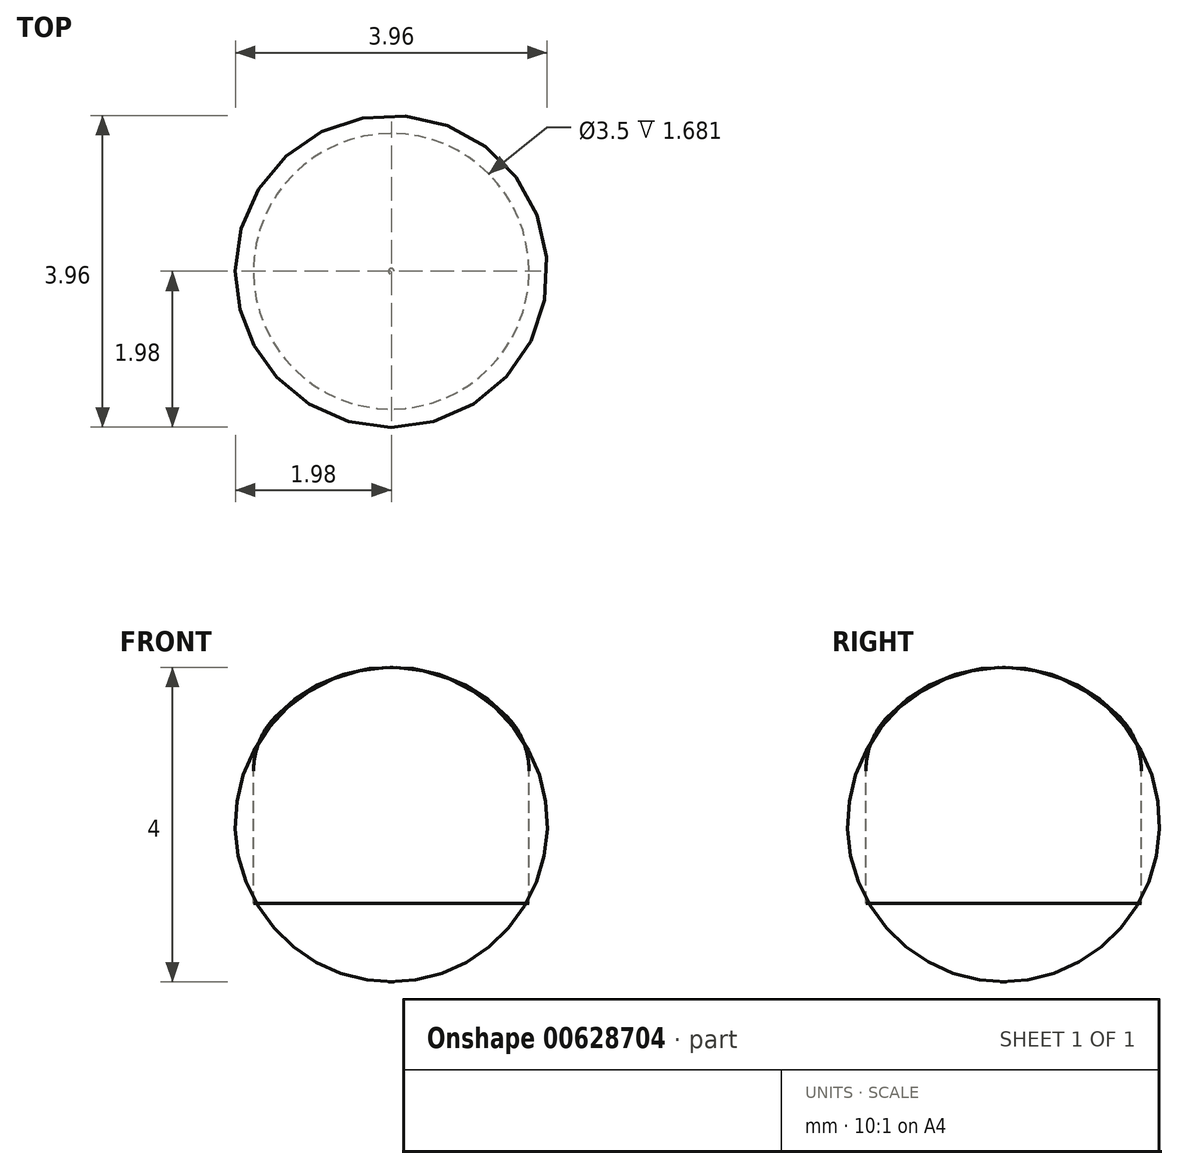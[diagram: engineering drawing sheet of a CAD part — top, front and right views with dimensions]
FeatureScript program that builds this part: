
annotation { "Feature Type Name" : "Feature", "Feature Type Description" : "" }
export const myFeature = defineFeature(function(context is Context, id is Id, definition is map)
    precondition{}
    {
        {
            var Q0;
            Q0=qCreatedBy(makeId("Front.planeOp"),FACE);
            var sketch = newSketch(context, id + "F0", { "sketchPlane" : qUnion([Q0])});
            skLineSegment(sketch, "E0", {"start": v(0, 19.78) * mm, "end": v(0, -18.06) * mm, "construction": true});
            skLineSegment(sketch, "E1", {"start": v(0, -1.5) * mm, "end": v(-1.75, -1.5) * mm});
            skLineSegment(sketch, "E2", {"start": v(-1.75, -1.5) * mm, "end": v(-1.75, 0.18) * mm});
            skArc(sketch, "E3", {"start": v(0, 1.5) * mm, "mid": v(-0.8, 1.34) * mm, "end": v(-1.48, 0.86) * mm});
            skLineSegment(sketch, "E4", {"start": v(0, 1.5) * mm, "end": v(0, -1.5) * mm});
            skPoint(sketch, "E5.visualSharp", {"position": v(-1.75, 0.5) * mm});
            skArc(sketch, "E5.filletArc", {"start": v(-1.48, 0.86) * mm, "mid": v(-1.68, 0.55) * mm, "end": v(-1.75, 0.18) * mm});
            skSolve(sketch);
        }
        {
            var Q0;
            Q0 = qSketchRegion(id + "F0", true);
            var Q1;
            Q1=sQuery(id+"F0.wireOp",EDGE,"E0");
            revolve(context, id + "F1", {"entities" : qUnion([Q0]), "axis" : qUnion([Q1]), "revolveType" : RevolveType.FULL});
        }
    });
